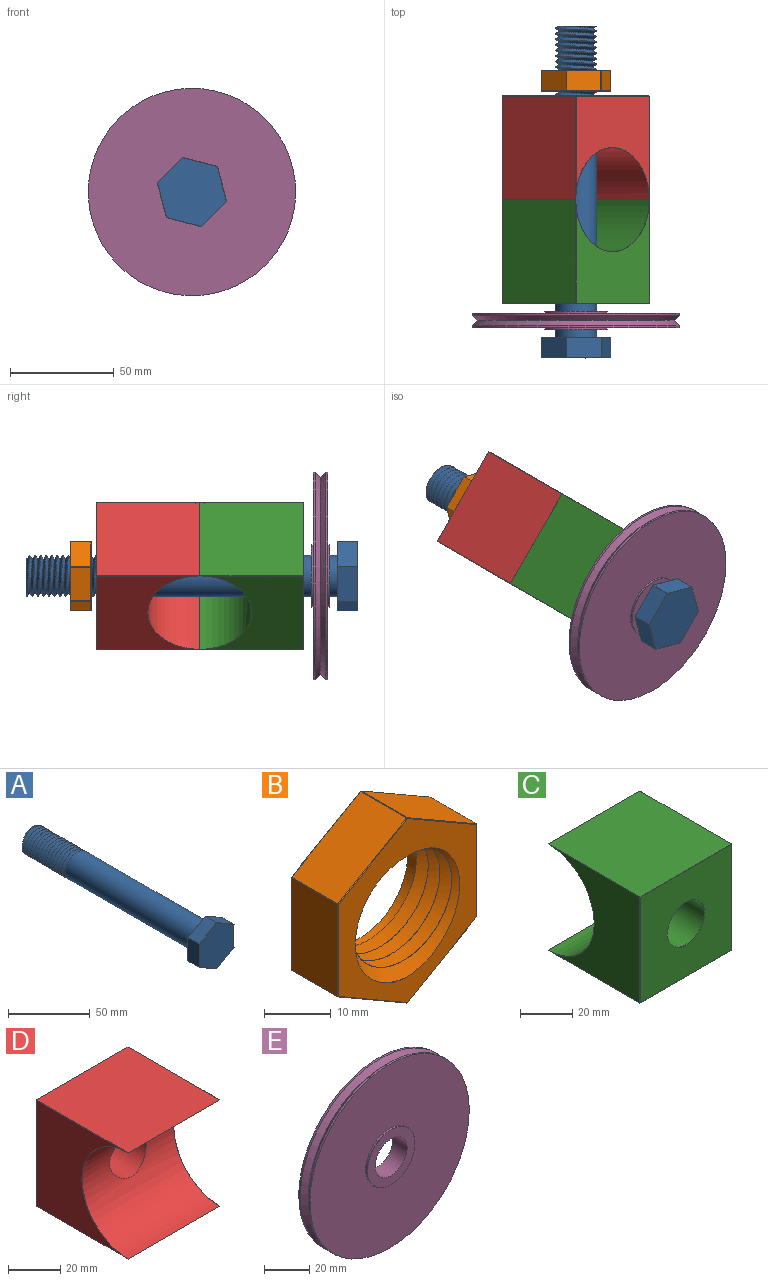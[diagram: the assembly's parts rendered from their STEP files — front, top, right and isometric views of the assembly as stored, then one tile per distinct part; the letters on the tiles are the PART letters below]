
ASSEMBLY  parts=5 mates=4
PART A: 57 faces, bbox 31.8x163.4x36.5 mm
  f0: cylinder r=10mm len=114.67mm, axis (0,-1,0), area 7003.1mm2, adj f1,f16,f17,f18,f26
  f1: cylinder r=10mm len=20mm, axis (0,-1,0), area 10.5mm2, adj f0,f2,f16,f17
  f2: cylinder r=10mm len=20mm, axis (0,-1,0), area 10.5mm2, adj f1,f3,f16,f17
  f3: cylinder r=10mm len=20mm, axis (0,-1,0), area 10.5mm2, adj f2,f4,f16,f17
  f4: cylinder r=10mm len=20mm, axis (0,-1,0), area 10.5mm2, adj f3,f5,f16,f17
  f5: cylinder r=10mm len=20mm, axis (0,-1,0), area 10.5mm2, adj f4,f6,f16,f17
  f6: cylinder r=10mm len=20mm, axis (0,-1,0), area 10.5mm2, adj f5,f7,f16,f17
  f7: cylinder r=10mm len=20mm, axis (0,-1,0), area 10.5mm2, adj f6,f8,f16,f17
  f8: cylinder r=10mm len=20mm, axis (0,-1,0), area 10.5mm2, adj f7,f9,f16,f17
  f9: cylinder r=10mm len=20mm, axis (0,-1,0), area 10.5mm2, adj f8,f10,f16,f17
  f10: cylinder r=10mm len=20mm, axis (0,-1,0), area 10.5mm2, adj f9,f11,f16,f17
  f11: cylinder r=10mm len=20mm, axis (0,-1,0), area 10.5mm2, adj f10,f12,f16,f17
  f12: cylinder r=10mm len=20mm, axis (0,-1,0), area 10.5mm2, adj f11,f13,f16,f17
  f13: cylinder r=10mm len=20mm, axis (0,-1,0), area 10.5mm2, adj f12,f14,f16,f17
  f14: cylinder r=10mm len=13.88mm, axis (0,-1,0), area 3mm2, adj f13,f15,f16,f17
  f15: plane 19.8x19.77mm, normal (0,1,0), area 255mm2, adj f14,f16,f17
  f16: bspline ~41.25x23.09mm, area 2075.8mm2, adj f0,f1,f2,f3,f4,f5,f6,f7
  f17: bspline ~40.36x23.09mm, area 2003.5mm2, adj f0,f1,f2,f3,f4,f5,f6,f7
  f18: plane 2.5x2.17mm, normal (0,0,1), area 2.7mm2, adj f0,f16,f17
  f19: plane 17.26x9.8mm, normal (-1,0,0), area 169.1mm2, adj f45,f50,f53,f56
  f20: plane 14.95x9.8mm, normal (-0.5,0,-0.87), area 169.1mm2, adj f42,f51,f52,f56
  f21: plane 14.95x9.8mm, normal (0.5,0,-0.87), area 169.1mm2, adj f32,f41,f42,f43
  f22: plane 17.26x9.8mm, normal (1,0,0), area 169.1mm2, adj f27,f31,f32,f33
  f23: plane 14.95x9.8mm, normal (0.5,0,0.87), area 169.1mm2, adj f27,f30,f34,f35
  f24: plane 14.95x9.8mm, normal (-0.5,0,0.87), area 169.1mm2, adj f35,f40,f44,f45
  f25: plane 34.52x29.89mm, normal (0,-1,0), area 773.8mm2, adj f30,f31,f40,f41,f50,f51
  f26: plane 34.52x29.89mm, normal (0,1,0), area 459.6mm2, adj f0,f33,f34,f43,f44,f52,f53
  f27: cylinder r=0.1mm len=9.8mm, axis (0,1,0), area 1mm2, adj f22,f23,f28,f29
  f28: sphere r=0.1mm, area 0mm2, adj f27,f30,f31
  f29: sphere r=0.1mm, area 0mm2, adj f27,f33,f34
  f30: cylinder r=0.1mm len=15mm, axis (0.87,0,-0.5), area 2.7mm2, adj f23,f25,f28,f36
  f31: cylinder r=0.1mm len=17.26mm, axis (0,0,-1), area 2.7mm2, adj f22,f25,f28,f37
  f32: cylinder r=0.1mm len=9.8mm, axis (0,1,0), area 1mm2, adj f21,f22,f37,f38
  f33: cylinder r=0.1mm len=17.26mm, axis (0,0,1), area 2.7mm2, adj f22,f26,f29,f38
  f34: cylinder r=0.1mm len=15mm, axis (-0.87,0,0.5), area 2.7mm2, adj f23,f26,f29,f39
  f35: cylinder r=0.1mm len=9.8mm, axis (0,1,0), area 1mm2, adj f23,f24,f36,f39
  f36: sphere r=0.1mm, area 0mm2, adj f30,f35,f40
  f37: sphere r=0.1mm, area 0mm2, adj f31,f32,f41
  f38: sphere r=0.1mm, area 0mm2, adj f32,f33,f43
  f39: sphere r=0.1mm, area 0mm2, adj f34,f35,f44
  f40: cylinder r=0.1mm len=15mm, axis (0.87,0,0.5), area 2.7mm2, adj f24,f25,f36,f46
  f41: cylinder r=0.1mm len=15mm, axis (-0.87,0,-0.5), area 2.7mm2, adj f21,f25,f37,f47
  f42: cylinder r=0.1mm len=9.8mm, axis (0,1,0), area 1mm2, adj f20,f21,f47,f48
  f43: cylinder r=0.1mm len=15mm, axis (0.87,0,0.5), area 2.7mm2, adj f21,f26,f38,f48
  f44: cylinder r=0.1mm len=15mm, axis (-0.87,0,-0.5), area 2.7mm2, adj f24,f26,f39,f49
  f45: cylinder r=0.1mm len=9.8mm, axis (0,1,0), area 1mm2, adj f19,f24,f46,f49
  f46: sphere r=0.1mm, area 0mm2, adj f40,f45,f50
  f47: sphere r=0.1mm, area 0mm2, adj f41,f42,f51
  f48: sphere r=0.1mm, area 0mm2, adj f42,f43,f52
  f49: sphere r=0.1mm, area 0mm2, adj f44,f45,f53
  f50: cylinder r=0.1mm len=17.26mm, axis (0,0,1), area 2.7mm2, adj f19,f25,f46,f54
  f51: cylinder r=0.1mm len=15mm, axis (-0.87,0,0.5), area 2.7mm2, adj f20,f25,f47,f54
  f52: cylinder r=0.1mm len=15mm, axis (0.87,0,-0.5), area 2.7mm2, adj f20,f26,f48,f55
  f53: cylinder r=0.1mm len=17.26mm, axis (0,0,-1), area 2.7mm2, adj f19,f26,f49,f55
  f54: sphere r=0.1mm, area 0mm2, adj f50,f51,f56
  f55: sphere r=0.1mm, area 0mm2, adj f52,f53,f56
  f56: cylinder r=0.1mm len=9.8mm, axis (0,1,0), area 1mm2, adj f19,f20,f54,f55
PART B: 42 faces, bbox 31.3x13.4x35.9 mm
  f0: cylinder r=10.01mm len=20.02mm, axis (0,1,0), area 85.1mm2, adj f1,f8,f9,f10,f11
  f1: plane 35.68x31.14mm, normal (0,-1,0), area 359.1mm2, adj f0,f10,f11,f15,f16,f25,f26,f35
  f2: plane 14.68x9.8mm, normal (-0.5,0,-0.87), area 166.1mm2, adj f30,f35,f38,f41
  f3: plane 14.68x9.8mm, normal (0.5,0,-0.87), area 166.1mm2, adj f27,f36,f37,f41
  f4: plane 16.95x9.8mm, normal (1,0,0), area 166.1mm2, adj f17,f26,f27,f28
  f5: plane 14.68x9.8mm, normal (0.5,0,0.87), area 166.1mm2, adj f12,f16,f17,f18
  f6: plane 14.68x9.8mm, normal (-0.5,0,0.87), area 166.1mm2, adj f12,f15,f19,f20
  f7: plane 16.95x9.8mm, normal (-1,0,0), area 166.1mm2, adj f20,f25,f29,f30
  f8: plane 33.9x29.36mm, normal (0,1,0), area 431.9mm2, adj f0,f18,f19,f28,f29,f37,f38
  f9: plane 2.5x2.16mm, normal (-1,0,0), area 2.7mm2, adj f0,f10,f11
  f10: bspline ~28.11x24.34mm, area 651.4mm2, adj f0,f1,f9,f11
  f11: bspline ~28.11x24.34mm, area 567.3mm2, adj f0,f1,f9,f10
  f12: cylinder r=0.1mm len=9.8mm, axis (0,1,0), area 1mm2, adj f5,f6,f13,f14
  f13: sphere r=0.1mm, area 0mm2, adj f12,f15,f16
  f14: sphere r=0.1mm, area 0mm2, adj f12,f18,f19
  f15: cylinder r=0.1mm len=14.73mm, axis (0.87,0,0.5), area 2.7mm2, adj f1,f6,f13,f21
  f16: cylinder r=0.1mm len=14.73mm, axis (0.87,0,-0.5), area 2.7mm2, adj f1,f5,f13,f22
  f17: cylinder r=0.1mm len=9.8mm, axis (0,1,0), area 1mm2, adj f4,f5,f22,f23
  f18: cylinder r=0.1mm len=14.73mm, axis (-0.87,0,0.5), area 2.7mm2, adj f5,f8,f14,f23
  f19: cylinder r=0.1mm len=14.73mm, axis (-0.87,0,-0.5), area 2.7mm2, adj f6,f8,f14,f24
  f20: cylinder r=0.1mm len=9.8mm, axis (0,1,0), area 1mm2, adj f6,f7,f21,f24
  f21: sphere r=0.1mm, area 0mm2, adj f15,f20,f25
  f22: sphere r=0.1mm, area 0mm2, adj f16,f17,f26
  f23: sphere r=0.1mm, area 0mm2, adj f17,f18,f28
  f24: sphere r=0.1mm, area 0mm2, adj f19,f20,f29
  f25: cylinder r=0.1mm len=16.95mm, axis (0,0,1), area 2.7mm2, adj f1,f7,f21,f31
  f26: cylinder r=0.1mm len=16.95mm, axis (0,0,-1), area 2.7mm2, adj f1,f4,f22,f32
  f27: cylinder r=0.1mm len=9.8mm, axis (0,1,0), area 1mm2, adj f3,f4,f32,f33
  f28: cylinder r=0.1mm len=16.95mm, axis (0,0,1), area 2.7mm2, adj f4,f8,f23,f33
  f29: cylinder r=0.1mm len=16.95mm, axis (0,0,-1), area 2.7mm2, adj f7,f8,f24,f34
  f30: cylinder r=0.1mm len=9.8mm, axis (0,1,0), area 1mm2, adj f2,f7,f31,f34
  f31: sphere r=0.1mm, area 0mm2, adj f25,f30,f35
  f32: sphere r=0.1mm, area 0mm2, adj f26,f27,f36
  f33: sphere r=0.1mm, area 0mm2, adj f27,f28,f37
  f34: sphere r=0.1mm, area 0mm2, adj f29,f30,f38
  f35: cylinder r=0.1mm len=14.73mm, axis (-0.87,0,0.5), area 2.7mm2, adj f1,f2,f31,f39
  f36: cylinder r=0.1mm len=14.73mm, axis (-0.87,0,-0.5), area 2.7mm2, adj f1,f3,f32,f39
  f37: cylinder r=0.1mm len=14.73mm, axis (0.87,0,0.5), area 2.7mm2, adj f3,f8,f33,f40
  f38: cylinder r=0.1mm len=14.73mm, axis (0.87,0,-0.5), area 2.7mm2, adj f2,f8,f34,f40
  f39: sphere r=0.1mm, area 0mm2, adj f35,f36,f41
  f40: sphere r=0.1mm, area 0mm2, adj f37,f38,f41
  f41: cylinder r=0.1mm len=9.8mm, axis (0,1,0), area 1mm2, adj f2,f3,f39,f40
PART C: 22 faces, bbox 50.1x50.1x50.3 mm
  f0: plane 49.9x49.8mm, normal (0,0,-1), area 2485mm2, adj f5,f9,f14,f19
  f1: plane 49.8x46.74mm, normal (1,0,0), area 1496.2mm2, adj f8,f9,f10,f11
  f2: plane 49.9x49.8mm, normal (0,0,1), area 2485mm2, adj f5,f10,f15,f20
  f3: plane 49.8x46.74mm, normal (-1,0,0), area 1496.2mm2, adj f16,f19,f20,f21
  f4: plane 49.8x49.8mm, normal (0,-1,0), area 2159.6mm2, adj f7,f11,f14,f15,f16
  f5: cylinder r=25mm len=50mm, axis (-1,0,0), area 3590.1mm2, adj f0,f2,f6,f8,f21
  f6: cylinder r=10mm len=26.99mm, axis (0,-1,0), area 1629.5mm2, adj f5,f7
  f7: cone r=10mm half-angle=45deg, axis (0,-1,0), area 8.9mm2, adj f4,f6
  f8: cone r=25.1mm half-angle=45deg, axis (1,0,0), area 10.7mm2, adj f1,f5,f9,f10
  f9: plane 49.97x0.17mm, normal (0.71,0,-0.71), area 6.8mm2, adj f0,f1,f8,f12
  f10: plane 49.97x0.17mm, normal (0.71,0,0.71), area 6.8mm2, adj f1,f2,f8,f13
  f11: plane 49.8x0.1mm, normal (0.71,-0.71,0), area 7mm2, adj f1,f4,f12,f13
  f12: plane 0.1x0.1mm, normal (0.58,-0.58,-0.58), area 0mm2, adj f9,f11,f14
  f13: plane 0.1x0.1mm, normal (0.58,-0.58,0.58), area 0mm2, adj f10,f11,f15
  f14: plane 49.8x0.1mm, normal (0,-0.71,-0.71), area 7mm2, adj f0,f4,f12,f17
  f15: plane 49.8x0.1mm, normal (0,-0.71,0.71), area 7mm2, adj f2,f4,f13,f18
  f16: plane 49.8x0.1mm, normal (-0.71,-0.71,0), area 7mm2, adj f3,f4,f17,f18
  f17: plane 0.1x0.1mm, normal (-0.58,-0.58,-0.58), area 0mm2, adj f14,f16,f19
  f18: plane 0.1x0.1mm, normal (-0.58,-0.58,0.58), area 0mm2, adj f15,f16,f20
  f19: plane 49.97x0.17mm, normal (-0.71,0,-0.71), area 6.8mm2, adj f0,f3,f17,f21
  f20: plane 49.97x0.17mm, normal (-0.71,0,0.71), area 6.8mm2, adj f2,f3,f18,f21
  f21: cone r=25mm half-angle=45deg, axis (-1,0,0), area 10.7mm2, adj f3,f5,f19,f20
PART D: 22 faces, bbox 50.1x50.1x50.3 mm
  f0: plane 49.8x49.8mm, normal (0,1,0), area 2159.6mm2, adj f7,f11,f14,f15,f16
  f1: plane 49.9x49.8mm, normal (0,0,-1), area 2485mm2, adj f5,f10,f15,f20
  f2: plane 49.9x49.8mm, normal (0,0,1), area 2485mm2, adj f5,f9,f14,f19
  f3: plane 49.8x46.74mm, normal (-1,0,0), area 1496.2mm2, adj f16,f19,f20,f21
  f4: plane 49.8x46.74mm, normal (1,0,0), area 1496.2mm2, adj f8,f9,f10,f11
  f5: cylinder r=25mm len=50mm, axis (-1,0,0), area 3590.1mm2, adj f1,f2,f6,f8,f21
  f6: cylinder r=10mm len=26.99mm, axis (0,1,0), area 1629.5mm2, adj f5,f7
  f7: cone r=10mm half-angle=45deg, axis (0,1,0), area 8.9mm2, adj f0,f6
  f8: cone r=25.1mm half-angle=45deg, axis (1,0,0), area 10.7mm2, adj f4,f5,f9,f10
  f9: plane 49.97x0.17mm, normal (0.71,0,0.71), area 6.8mm2, adj f2,f4,f8,f12
  f10: plane 49.97x0.17mm, normal (0.71,0,-0.71), area 6.8mm2, adj f1,f4,f8,f13
  f11: plane 49.8x0.1mm, normal (0.71,0.71,0), area 7mm2, adj f0,f4,f12,f13
  f12: plane 0.1x0.1mm, normal (0.58,0.58,0.58), area 0mm2, adj f9,f11,f14
  f13: plane 0.1x0.1mm, normal (0.58,0.58,-0.58), area 0mm2, adj f10,f11,f15
  f14: plane 49.8x0.1mm, normal (0,0.71,0.71), area 7mm2, adj f0,f2,f12,f17
  f15: plane 49.8x0.1mm, normal (0,0.71,-0.71), area 7mm2, adj f0,f1,f13,f18
  f16: plane 49.8x0.1mm, normal (-0.71,0.71,0), area 7mm2, adj f0,f3,f17,f18
  f17: plane 0.1x0.1mm, normal (-0.58,0.58,0.58), area 0mm2, adj f14,f16,f19
  f18: plane 0.1x0.1mm, normal (-0.58,0.58,-0.58), area 0mm2, adj f15,f16,f20
  f19: plane 49.97x0.17mm, normal (-0.71,0,0.71), area 6.8mm2, adj f2,f3,f17,f21
  f20: plane 49.97x0.17mm, normal (-0.71,0,-0.71), area 6.8mm2, adj f1,f3,f18,f21
  f21: cone r=25mm half-angle=45deg, axis (-1,0,0), area 10.7mm2, adj f3,f5,f19,f20
PART E: 13 faces, bbox 100x9x100 mm
  f0: cylinder r=50mm len=100mm, axis (0,1,0), area 314.2mm2, adj f1,f2
  f1: plane 100x100mm, normal (0,1,0), area 7146.3mm2, adj f0,f9
  f2: cone r=47.5mm half-angle=45deg, axis (0,1,0), area 1083mm2, adj f0,f6
  f3: cylinder r=10mm len=20mm, axis (0,1,0), area 565.5mm2, adj f8,f10
  f4: cylinder r=50mm len=100mm, axis (0,-1,0), area 314.2mm2, adj f5,f6
  f5: plane 100x100mm, normal (0,-1,0), area 7147.1mm2, adj f4,f7
  f6: cone r=47.5mm half-angle=45deg, axis (0,-1,0), area 1083mm2, adj f2,f4
  f7: cylinder r=15mm len=30mm, axis (0,1,0), area 84.8mm2, adj f5,f12
  f8: plane 29.8x29.8mm, normal (0,-1,0), area 383.3mm2, adj f3,f12
  f9: cylinder r=15.01mm len=30.02mm, axis (0,-1,0), area 84.9mm2, adj f1,f11
  f10: plane 29.82x29.82mm, normal (0,1,0), area 384.1mm2, adj f3,f11
  f11: torus R=14.91mm, axis (0,1,0), area 14.8mm2, adj f9,f10
  f12: torus R=14.9mm, axis (0,-1,0), area 14.8mm2, adj f7,f8
PLACE A rot(axis=(0,1,0),45deg) t=(-51.23,-1.4,43.64)mm
PLACE B rot(axis=(0,1,0),45deg) t=(-51.23,127.26,43.64)mm
PLACE C rot(axis=(0,-1,0),45deg) t=(-51.23,64.82,43.64)mm
PLACE D rot(axis=(0,-1,0),45deg) t=(-51.23,64.87,43.64)mm
PLACE E rot(axis=(0,1,0),45deg) t=(-51.23,10.16,43.64)mm
MATE slider E.f3 <-> A.f0  axis (0,-1,0) through (-51.23,2.16,43.64)mm
MATE slider C.f6 <-> A.f0  axis (0,-1,0) through (-51.23,14.82,43.64)mm
MATE slider D.f6 <-> A.f0  axis (0,1,0) through (-51.23,101.19,43.64)mm
MATE slider A.f0 <-> B.f0  axis (0,-1,0) through (-51.23,148.6,43.64)mm
